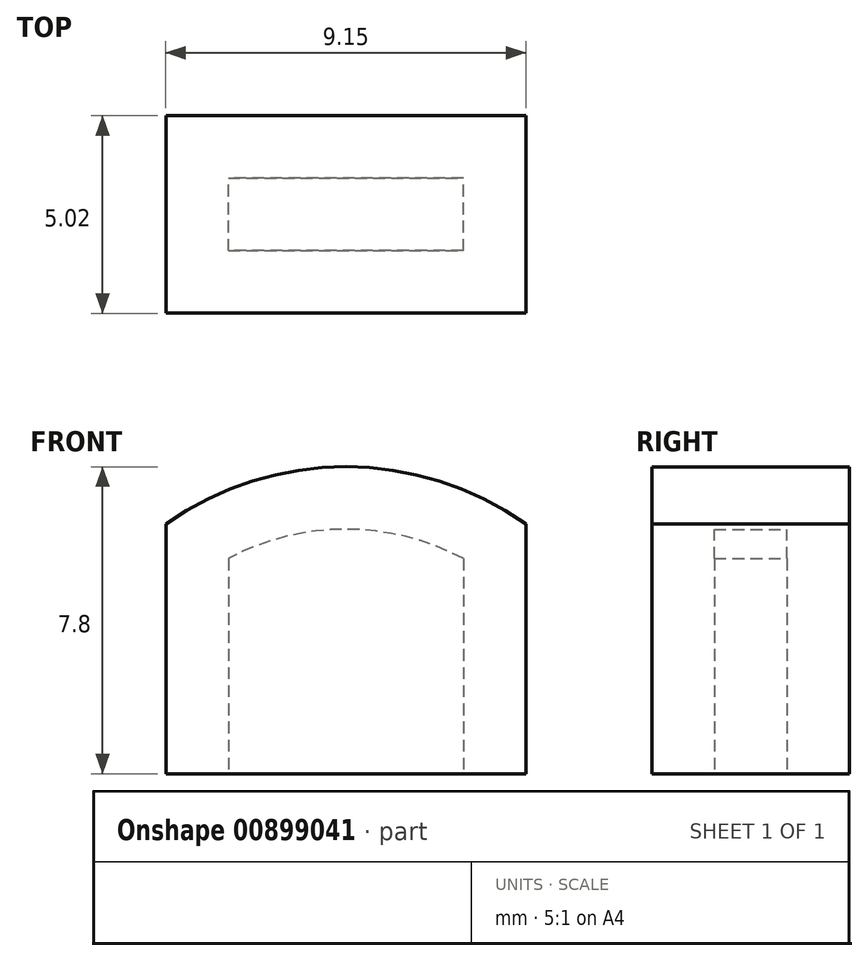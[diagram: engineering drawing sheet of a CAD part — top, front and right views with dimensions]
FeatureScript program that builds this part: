
annotation { "Feature Type Name" : "Feature", "Feature Type Description" : "" }
export const myFeature = defineFeature(function(context is Context, id is Id, definition is map)
    precondition{}
    {
        {
            var Q0;
            Q0=qCreatedBy(makeId("Front.planeOp"),FACE);
            var sketch = newSketch(context, id + "F0", { "sketchPlane" : qUnion([Q0])});
            skLineSegment(sketch, "E0.bottom", {"start": v(-4.86, 6.35) * mm, "end": v(4.29, 6.35) * mm});
            skLineSegment(sketch, "E0.top", {"start": v(-4.86, 0) * mm, "end": v(4.29, 0) * mm});
            skLineSegment(sketch, "E0.left", {"start": v(-4.86, 6.35) * mm, "end": v(-4.86, 0) * mm});
            skLineSegment(sketch, "E0.right", {"start": v(4.29, 6.35) * mm, "end": v(4.29, 0) * mm});
            skArc(sketch, "E1", {"start": v(4.29, 6.35) * mm, "mid": v(-0.28, 7.8) * mm, "end": v(-4.86, 6.35) * mm});
            skSolve(sketch);
        }
        {
            var Q0;
            {var subQ0=sQuery(id+"F0.wireOp",EDGE,"E0.bottom");Q0=makeQuery(id+"F0.imprint","IMPRINT",FACE,{"disambiguationData":[TD([[makeQuery(id+"F0.imprint","IMPRINT",EDGE,{"derivedFrom":subQ0}),-1.0]])]});}
            var Q1;
            {var subQ0=sQuery(id+"F0.wireOp",EDGE,"E0.bottom");Q1=makeQuery(id+"F0.imprint","IMPRINT",FACE,{"disambiguationData":[TD([[makeQuery(id+"F0.imprint","IMPRINT",EDGE,{"derivedFrom":subQ0}),1.0]])]});}
            var Q2;
            Q2=makeQuery(id+"F0.imprint","IMPRINT",FACE,{"disambiguationData":[TD([[makeQuery(id+"F0.imprint","IMPRINT",EDGE,{"derivedFrom":sQuery(id+"F0.wireOp",EDGE,"E0.top")}),1.0]])]});
            extrude(context, id + "F1", {"entities" : qUnion([Q0, Q1, Q2]), "depth" : 5.02 * mm, "offsetDistance" : 25.4 * mm});
        }
        {
            var Q0;
            Q0=makeQuery(id+"F1.opExtrude","SWEPT_FACE",FACE,{"disambiguationData":[OSD([sQuery(id+"F0.wireOp",EDGE,"E0.top")])]});
            shell(context, id + "F2", {"entities" : qUnion([Q0]), "thickness" : 1.59 * mm});
        }
    });
